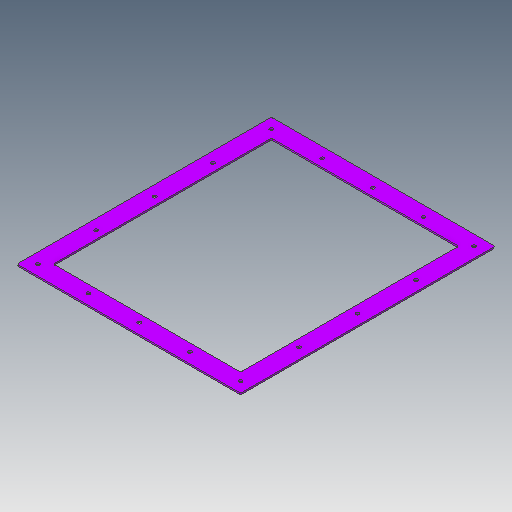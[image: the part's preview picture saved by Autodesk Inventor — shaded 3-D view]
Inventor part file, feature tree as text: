
AUTODESK INVENTOR PART (.ipt)
format: ipt  version: 2017 (Build 210142000, 142)  size: 150,528 bytes
history: native  units: mm
features: extrude x2, sketch x2
ambient origin geometry x8: Origin, YZ Plane, XZ Plane, XY Plane, X Axis, Y Axis, Z Axis, Center Point
bodies: Solid1 (feature_tree)
feature tree (4):
  extrude  "Extrusion1"  Depth=838.2mm
  extrude  "Extrusion2"  Depth=5.0mm
  sketch  "Sketch1"  dims[d0=736.6mm d1=838.2mm]
  sketch  "Sketch2"  dims[d2=60.0mm d4=5.0mm d6=5.0mm d7=0.0mm d8=0.0mm d9=0.0mm]
